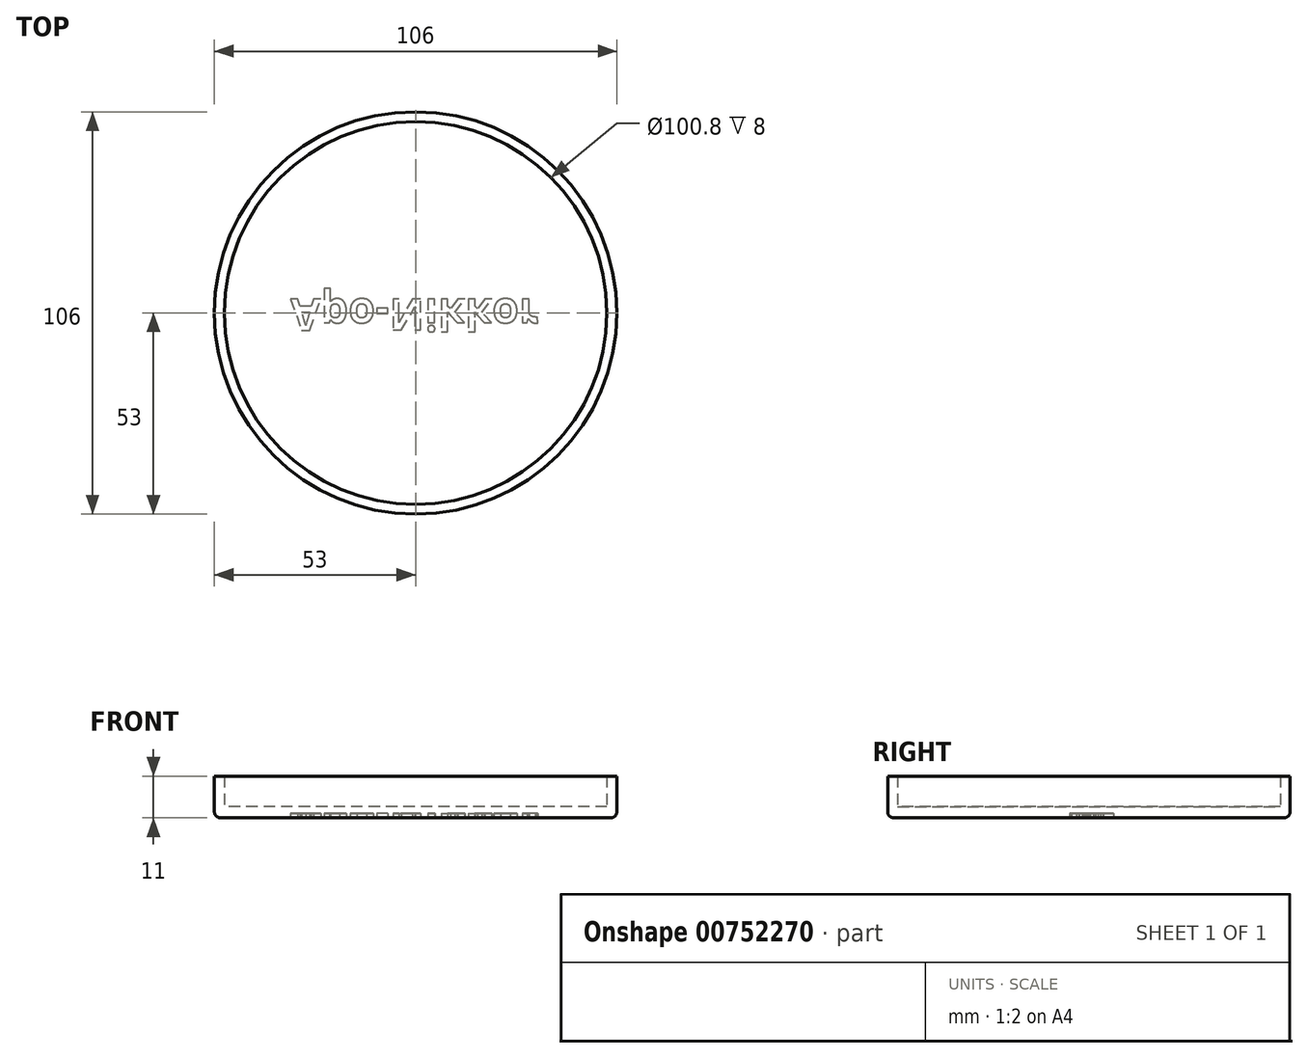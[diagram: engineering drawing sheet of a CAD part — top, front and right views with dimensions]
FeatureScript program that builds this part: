
annotation { "Feature Type Name" : "Feature", "Feature Type Description" : "" }
export const myFeature = defineFeature(function(context is Context, id is Id, definition is map)
    precondition{}
    {
        {
            var Q0;
            Q0=qCreatedBy(makeId("Top.planeOp"),FACE);
            var sketch = newSketch(context, id + "F0", { "sketchPlane" : qUnion([Q0])});
            skCircle(sketch, "E0", {"center": v(0, 0) * mm, "radius": 53 * mm});
            skSolve(sketch);
        }
        {
            var Q0;
            Q0=makeQuery(id+"F0.imprint","IMPRINT",FACE,{"disambiguationData":[TD([[makeQuery(id+"F0.imprint","IMPRINT",EDGE,{"derivedFrom":sQuery(id+"F0.wireOp",EDGE,"E0")}),1.0]])]});
            extrude(context, id + "F1", {"entities" : qUnion([Q0]), "depth" : 3 * mm, "offsetDistance" : 25 * mm});
        }
        {
            var Q0;
            Q0=makeQuery(id+"F1.opExtrude","CAP_FACE",FACE,{"disambiguationData":[OSD([sQuery(id+"F0.wireOp",EDGE,"E0")])],"isStart":false});
            var sketch = newSketch(context, id + "F2", { "sketchPlane" : qUnion([Q0])});
            skCircle(sketch, "E1", {"center": v(0, 0) * mm, "radius": 53 * mm});
            skCircle(sketch, "E2.0", {"center": v(0, 0) * mm, "radius": 50.4 * mm});
            skSolve(sketch);
        }
        {
            var Q0;
            Q0=makeQuery(id+"F2.imprint","IMPRINT",FACE,{"disambiguationData":[TD([[makeQuery(id+"F2.imprint","IMPRINT",EDGE,{"derivedFrom":sQuery(id+"F2.wireOp",EDGE,"E1")}),1.0]])]});
            extrude(context, id + "F3", {"entities" : qUnion([Q0]), "operationType" : NewBodyOperationType.ADD, "depth" : 8 * mm, "offsetDistance" : 25 * mm});
        }
        {
            var Q0;
            Q0=makeQuery(id+"F1.opExtrude","CAP_FACE",FACE,{"disambiguationData":[OSD([sQuery(id+"F0.wireOp",EDGE,"E0")])],"isStart":true});
            var sketch = newSketch(context, id + "F4", { "sketchPlane" : qUnion([Q0])});
            skText(sketch, "E3", { "text": "Apo-Nikkor", "fontName": "OpenSans-Bold.ttf"});
            const initialGuessF4  = {"E3": [-0.0329, -0.0037, 1, 0, 0.00826]};
            skSetInitialGuess(sketch, initialGuessF4);
            skSolve(sketch);
        }
        {
            var Q0;
            Q0 = qSketchRegion(id + "F4", true);
            extrude(context, id + "F5", {"entities" : qUnion([Q0]), "operationType" : NewBodyOperationType.REMOVE, "oppositeDirection" : true, "depth" : 1.2 * mm, "offsetDistance" : 25 * mm});
        }
        {
            var Q0;
            Q0=makeQuery(id+"F1.opExtrude","CAP_EDGE",EDGE,{"disambiguationData":[OSD([sQuery(id+"F0.wireOp",EDGE,"E0")])],"isStart":true});
            fillet(context, id + "F6", {"entities" : qUnion([Q0]), "radius" : 1.6 * mm, "tangentPropagation" : true, "allowEdgeOverflow" : false});
        }
    });
